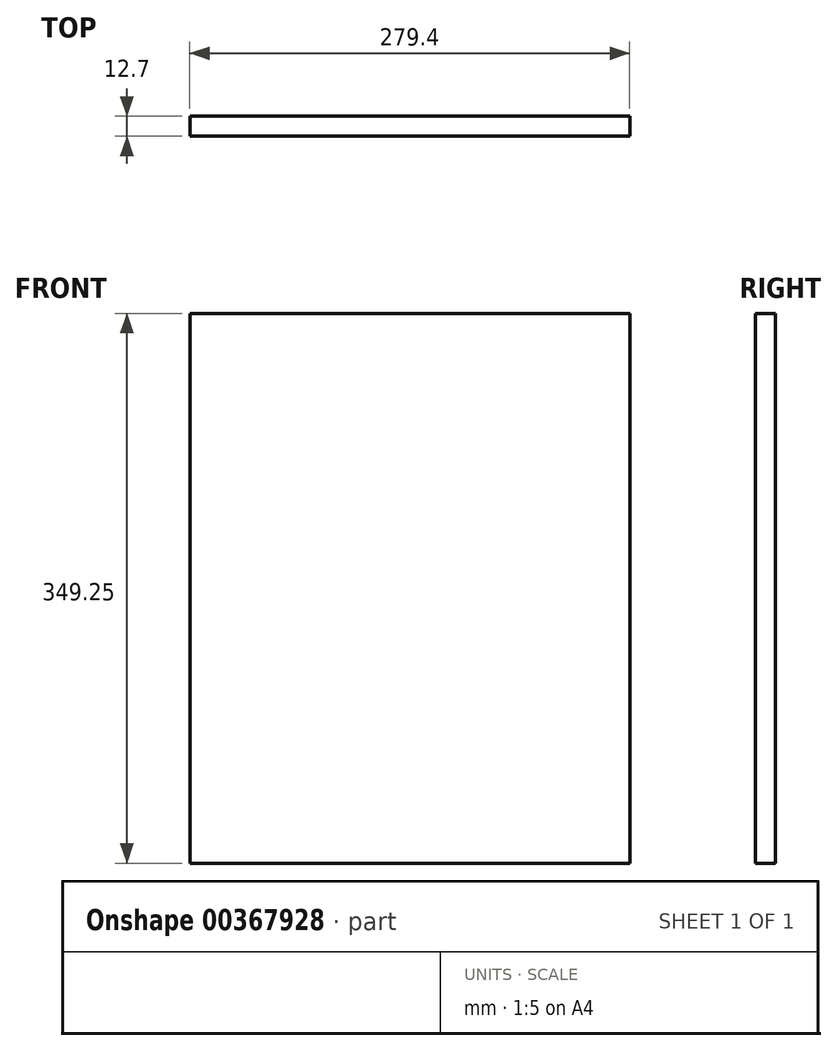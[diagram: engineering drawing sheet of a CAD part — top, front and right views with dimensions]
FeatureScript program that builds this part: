
annotation { "Feature Type Name" : "Feature", "Feature Type Description" : "" }
export const myFeature = defineFeature(function(context is Context, id is Id, definition is map)
    precondition{}
    {
        {
            var Q0;
            Q0=qCreatedBy(makeId("Front.planeOp"),FACE);
            var sketch = newSketch(context, id + "F0", { "sketchPlane" : qUnion([Q0])});
            skLineSegment(sketch, "E0.bottom", {"start": v(-159.23, 195.77) * mm, "end": v(120.17, 195.77) * mm});
            skLineSegment(sketch, "E0.top", {"start": v(-159.23, -153.48) * mm, "end": v(120.17, -153.48) * mm});
            skLineSegment(sketch, "E0.left", {"start": v(-159.23, 195.77) * mm, "end": v(-159.23, -153.48) * mm});
            skLineSegment(sketch, "E0.right", {"start": v(120.17, 195.77) * mm, "end": v(120.17, -153.48) * mm});
            skSolve(sketch);
        }
        {
            var Q0;
            Q0=makeQuery(id+"F0.imprint","IMPRINT",FACE,{"disambiguationData":[TD([[makeQuery(id+"F0.imprint","IMPRINT",EDGE,{"derivedFrom":sQuery(id+"F0.wireOp",EDGE,"E0.bottom")}),-1.0]])]});
            extrude(context, id + "F1", {"entities" : qUnion([Q0]), "depth" : 12.7 * mm});
        }
    });
